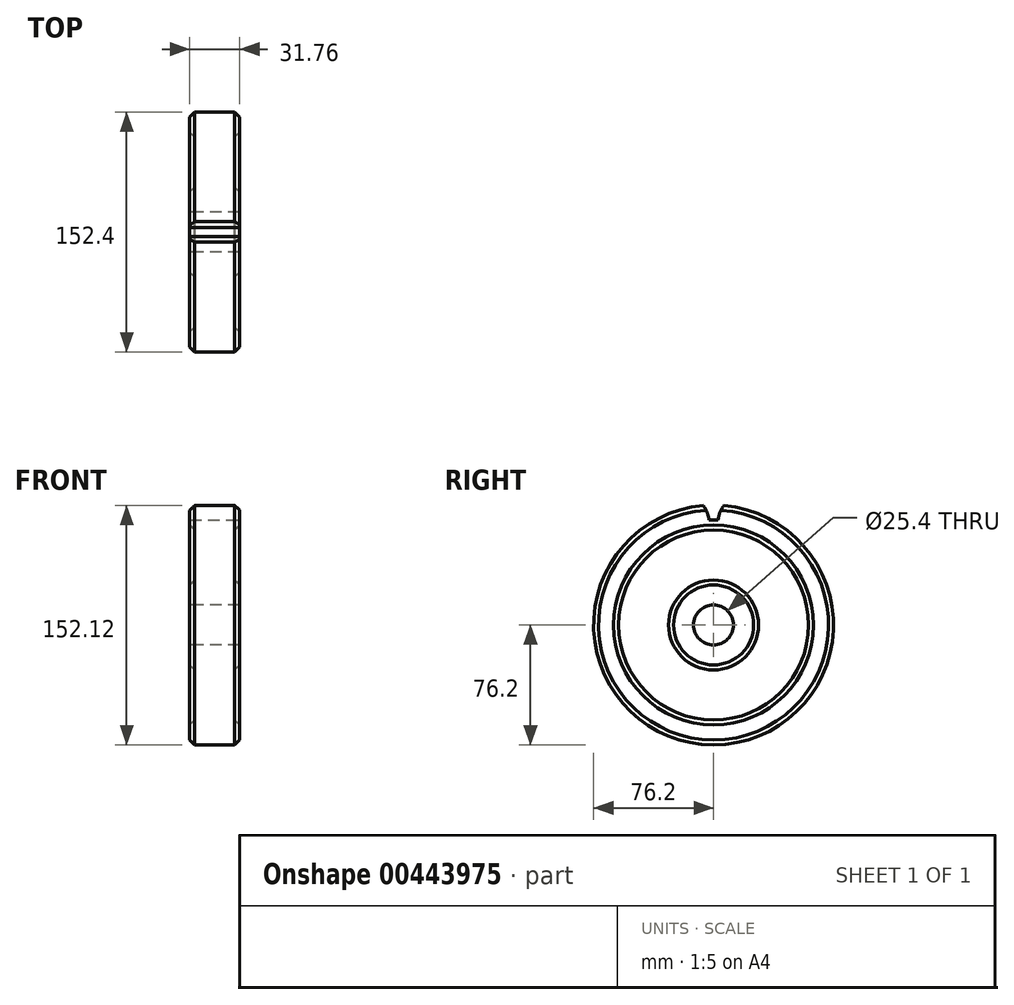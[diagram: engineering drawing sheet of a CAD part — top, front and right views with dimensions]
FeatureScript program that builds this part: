
annotation { "Feature Type Name" : "Feature", "Feature Type Description" : "" }
export const myFeature = defineFeature(function(context is Context, id is Id, definition is map)
    precondition{}
    {
        {
            var Q0;
            Q0=qCreatedBy(makeId("Top.planeOp"),FACE);
            var sketch = newSketch(context, id + "F0", { "sketchPlane" : qUnion([Q0])});
            skLineSegment(sketch, "E0", {"start": v(0, 0) * mm, "end": v(0, 63.5) * mm});
            skLineSegment(sketch, "E1", {"start": v(0, 63.5) * mm, "end": v(12.7, 63.5) * mm});
            skLineSegment(sketch, "E2", {"start": v(12.7, 63.5) * mm, "end": v(15.88, 60.33) * mm});
            skLineSegment(sketch, "E3", {"start": v(15.88, 60.33) * mm, "end": v(15.88, 50.8) * mm});
            skLineSegment(sketch, "E4", {"start": v(15.88, 50.8) * mm, "end": v(12.7, 47.63) * mm});
            skLineSegment(sketch, "E5", {"start": v(12.7, 47.63) * mm, "end": v(12.7, 15.87) * mm});
            skLineSegment(sketch, "E6", {"start": v(12.7, 15.87) * mm, "end": v(15.88, 12.7) * mm});
            skLineSegment(sketch, "E7", {"start": v(15.88, 12.7) * mm, "end": v(15.88, 0) * mm});
            skLineSegment(sketch, "E8", {"start": v(15.88, 0) * mm, "end": v(0, 0) * mm});
            skLineSegment(sketch, "E9.MirrorCS", {"start": v(0, 63.5) * mm, "end": v(-12.7, 63.5) * mm});
            skLineSegment(sketch, "E10.MirrorCS", {"start": v(-12.7, 63.5) * mm, "end": v(-15.88, 60.33) * mm});
            skLineSegment(sketch, "E11.MirrorCS", {"start": v(-15.88, 60.33) * mm, "end": v(-15.88, 50.8) * mm});
            skLineSegment(sketch, "E12.MirrorCS", {"start": v(-15.87, 50.8) * mm, "end": v(-12.7, 47.62) * mm});
            skLineSegment(sketch, "E13.MirrorCS", {"start": v(-12.7, 47.63) * mm, "end": v(-12.7, 15.87) * mm});
            skLineSegment(sketch, "E14.MirrorCS", {"start": v(-12.7, 15.87) * mm, "end": v(-15.88, 12.7) * mm});
            skLineSegment(sketch, "E15.MirrorCS", {"start": v(-15.88, 12.7) * mm, "end": v(-15.88, 0) * mm});
            skLineSegment(sketch, "E16.MirrorCS", {"start": v(-15.88, 0) * mm, "end": v(0, 0) * mm});
            skLineSegment(sketch, "E17", {"start": v(0, 0) * mm, "end": v(0, -12.7) * mm});
            skLineSegment(sketch, "E18", {"start": v(0, -12.7) * mm, "end": v(19.96, -12.7) * mm});
            skSolve(sketch);
        }
        {
            var Q0;
            Q0=makeQuery(id+"F0.imprint","IMPRINT",FACE,{"disambiguationData":[TD([[makeQuery(id+"F0.imprint","IMPRINT",EDGE,{"derivedFrom":sQuery(id+"F0.wireOp",EDGE,"E0")}),1.0]])]});
            var Q1;
            Q1=makeQuery(id+"F0.imprint","IMPRINT",FACE,{"disambiguationData":[TD([[makeQuery(id+"F0.imprint","IMPRINT",EDGE,{"derivedFrom":sQuery(id+"F0.wireOp",EDGE,"E0")}),-1.0]])]});
            var Q2;
            Q2=sQuery(id+"F0.wireOp",EDGE,"E18");
            revolve(context, id + "F1", {"entities" : qUnion([Q0, Q1]), "axis" : qUnion([Q2]), "revolveType" : RevolveType.FULL});
        }
        {
            var Q0;
            Q0=makeQuery(id+"F1.opRevolve","SWEPT_FACE",FACE,{"disambiguationData":[OSD([sQuery(id+"F0.wireOp",EDGE,"E3")])]});
            var sketch = newSketch(context, id + "F2", { "sketchPlane" : qUnion([Q0])});
            skLineSegment(sketch, "E19", {"start": v(-12.7, 0) * mm, "end": v(-12.7, 92.35) * mm});
            skLineSegment(sketch, "E20", {"start": v(-12.7, 66.68) * mm, "end": v(-9.84, 66.68) * mm});
            skArc(sketch, "E21", {"start": v(-6.16, 75.92) * mm, "mid": v(-8.62, 71.54) * mm, "end": v(-9.84, 66.68) * mm});
            skArc(sketch, "E22.0", {"start": v(-6.16, 75.92) * mm, "mid": v(-12.7, 76.2) * mm, "end": v(-19.24, 75.92) * mm});
            skLineSegment(sketch, "E23.MirrorCS", {"start": v(-12.7, 66.68) * mm, "end": v(-15.56, 66.68) * mm});
            skArc(sketch, "E24.MirrorCS", {"start": v(-19.24, 75.92) * mm, "mid": v(-16.78, 71.54) * mm, "end": v(-15.56, 66.68) * mm});
            skSolve(sketch);
        }
        {
            var Q0;
            {var subQ0=sQuery(id+"F2.wireOp",EDGE,"E23.MirrorCS");Q0=makeQuery(id+"F2.imprint","IMPRINT",FACE,{"disambiguationData":[TD([[makeQuery(id+"F2.imprint","IMPRINT",EDGE,{"derivedFrom":subQ0}),-1.0]])]});}
            var Q1;
            {var subQ0=sQuery(id+"F2.wireOp",EDGE,"E20");Q1=makeQuery(id+"F2.imprint","IMPRINT",FACE,{"disambiguationData":[TD([[makeQuery(id+"F2.imprint","IMPRINT",EDGE,{"derivedFrom":subQ0}),1.0]])]});}
            var Q2;
            {var subQ0=sQuery(id+"F2.wireOp",EDGE,"E22.0");var subQ5=sQuery(id+"F2.wireOp",EDGE,"E21");var subQ6=makeQuery(id+"F2.imprint","INTERSECT",VERTEX,{"derivedFrom":[subQ5,subQ0]});Q2=makeQuery(id+"F2.imprint","IMPRINT",FACE,{"disambiguationData":[TD([[makeQuery(id+"F2.imprint","IMPRINT",EDGE,{"disambiguationData":[TD([[subQ6,-1.0]])],"derivedFrom":subQ0}),1.0]])]});}
            var Q3;
            {var subQ0=sQuery(id+"F2.wireOp",EDGE,"E22.0");var subQ5=sQuery(id+"F2.wireOp",EDGE,"E24.MirrorCS");var subQ6=makeQuery(id+"F2.imprint","INTERSECT",VERTEX,{"derivedFrom":[subQ0,subQ5]});Q3=makeQuery(id+"F2.imprint","IMPRINT",FACE,{"disambiguationData":[TD([[makeQuery(id+"F2.imprint","IMPRINT",EDGE,{"disambiguationData":[TD([[subQ6,1.0]])],"derivedFrom":subQ0}),1.0]])]});}
            extrude(context, id + "F3", {"entities" : qUnion([Q0, Q1, Q2, Q3]), "operationType" : NewBodyOperationType.REMOVE, "endBound" : BoundingType.THROUGH_ALL, "oppositeDirection" : true, "depth" : 25.4 * mm});
        }
    });
